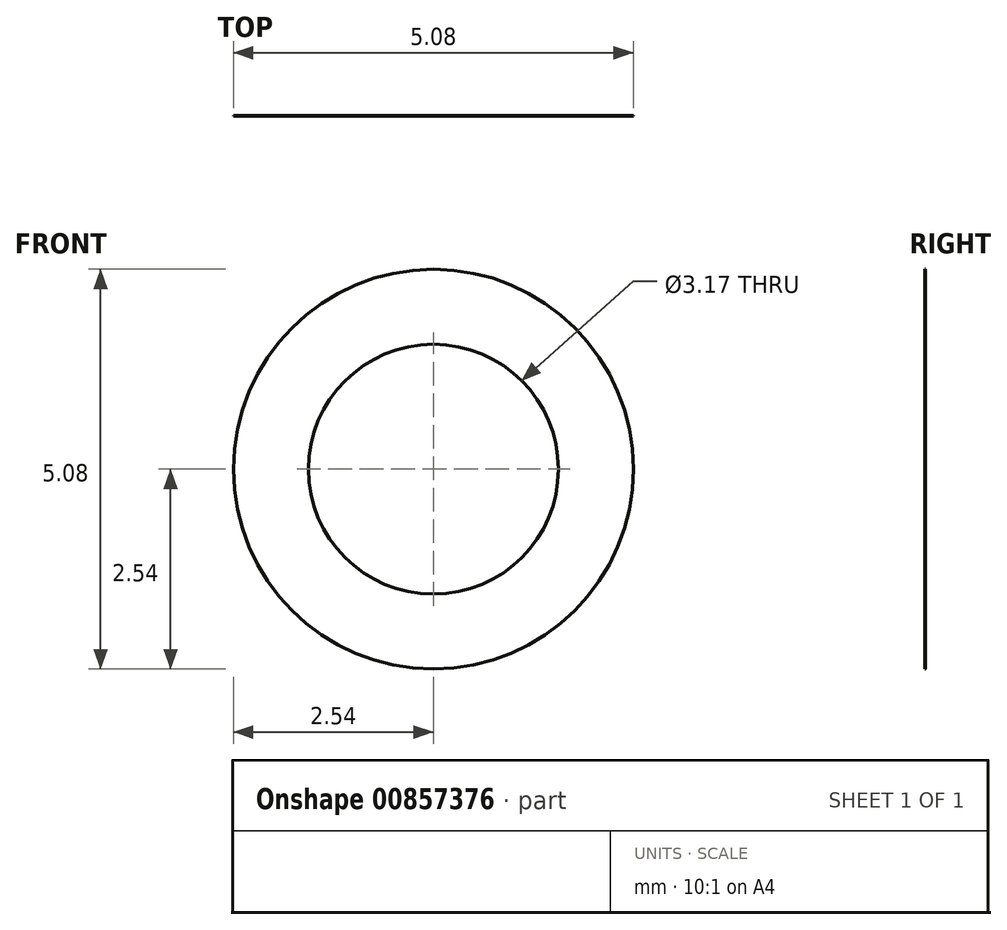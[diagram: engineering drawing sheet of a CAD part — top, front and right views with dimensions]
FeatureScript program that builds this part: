
annotation { "Feature Type Name" : "Feature", "Feature Type Description" : "" }
export const myFeature = defineFeature(function(context is Context, id is Id, definition is map)
    precondition{}
    {
        {
            var Q0;
            Q0=qCreatedBy(makeId("Front.planeOp"),FACE);
            var sketch = newSketch(context, id + "F0", { "sketchPlane" : qUnion([Q0])});
            skCircle(sketch, "E0", {"center": v(0, 0) * mm, "radius": 1.59 * mm});
            skCircle(sketch, "E1", {"center": v(0, 0) * mm, "radius": 2.54 * mm});
            skSolve(sketch);
        }
        {
            var Q0;
            Q0 = qSketchRegion(id + "F0", true);
            extrude(context, id + "F1", {"entities" : qUnion([Q0]), "depth" : 1 / 203.2 * mm, "offsetDistance" : 25.4 * mm});
        }
    });
